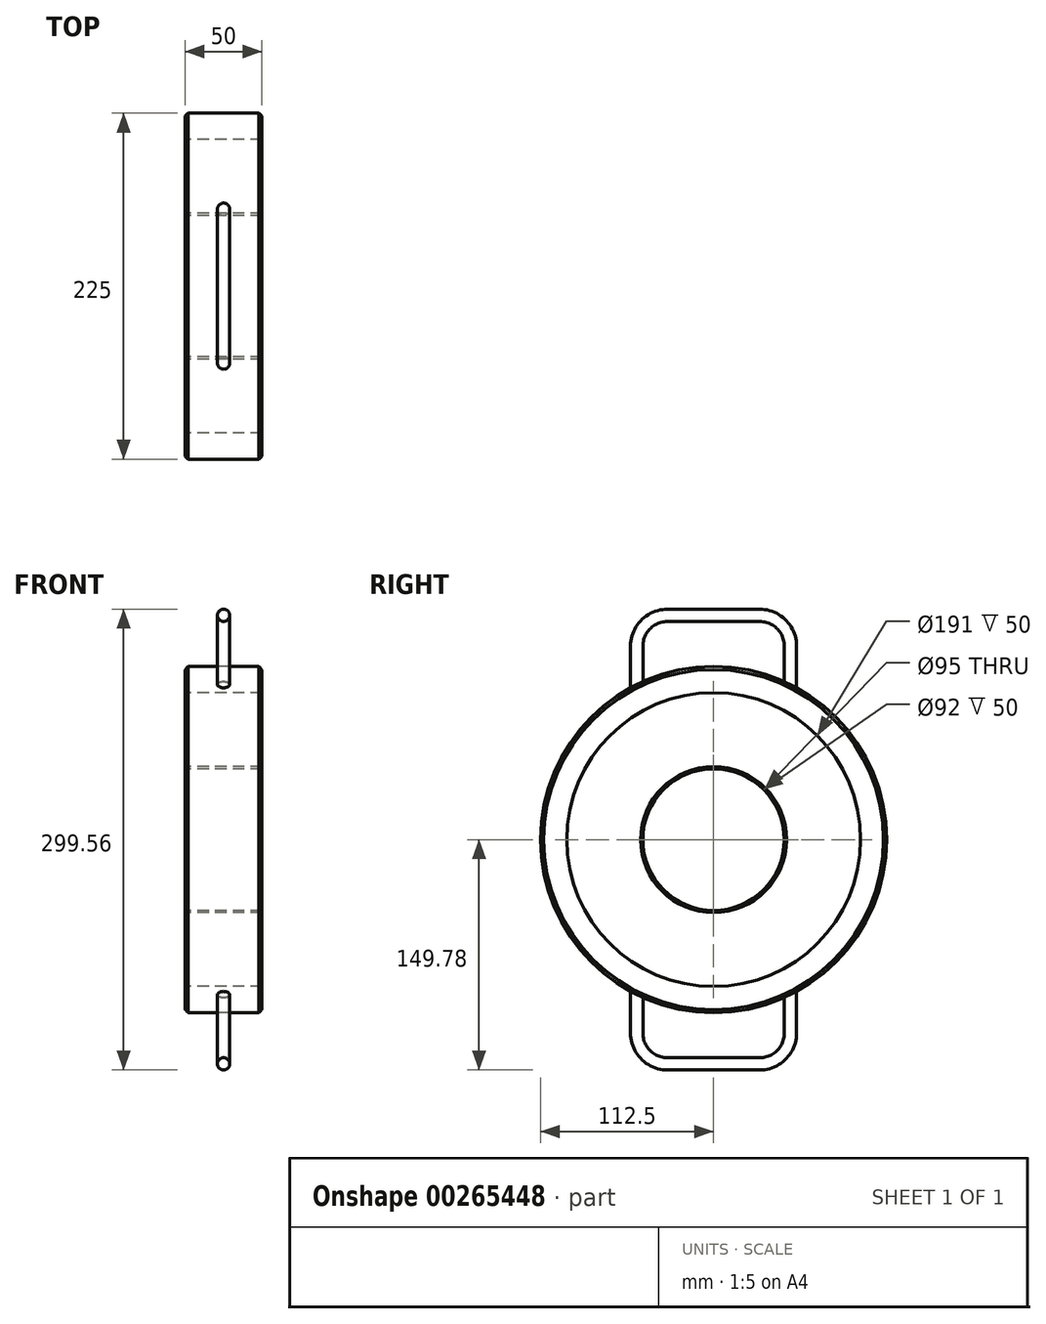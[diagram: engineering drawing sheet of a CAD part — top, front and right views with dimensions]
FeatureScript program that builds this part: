
annotation { "Feature Type Name" : "Feature", "Feature Type Description" : "" }
export const myFeature = defineFeature(function(context is Context, id is Id, definition is map)
    precondition{}
    {
        {
            var Q0;
            Q0=qCreatedBy(makeId("Front.planeOp"),FACE);
            var sketch = newSketch(context, id + "F0", { "sketchPlane" : qUnion([Q0])});
            skLineSegment(sketch, "E0", {"start": v(-48.97, 0) * mm, "end": v(48.97, 0) * mm, "construction": true});
            skLineSegment(sketch, "E1.bottom", {"start": v(-25, 47.5) * mm, "end": v(25, 47.5) * mm});
            skLineSegment(sketch, "E1.top", {"start": v(-25, 46) * mm, "end": v(25, 46) * mm});
            skLineSegment(sketch, "E1.left", {"start": v(-25, 47.5) * mm, "end": v(-25, 46) * mm});
            skLineSegment(sketch, "E1.right", {"start": v(25, 47.5) * mm, "end": v(25, 46) * mm});
            skLineSegment(sketch, "E2", {"start": v(0, 12.38) * mm, "end": v(0, -12.38) * mm, "construction": true});
            skSolve(sketch);
        }
        {
            var Q0;
            Q0=makeQuery(id+"F0.imprint","IMPRINT",FACE,{"disambiguationData":[TD([[makeQuery(id+"F0.imprint","IMPRINT",EDGE,{"derivedFrom":sQuery(id+"F0.wireOp",EDGE,"E1.bottom")}),-1.0]])]});
            var Q1;
            Q1=sQuery(id+"F0.wireOp",EDGE,"E0");
            revolve(context, id + "F1", {"entities" : qUnion([Q0]), "axis" : qUnion([Q1]), "revolveType" : RevolveType.FULL});
        }
        {
            var Q0;
            Q0=qCreatedBy(makeId("Front.planeOp"),FACE);
            var sketch = newSketch(context, id + "F2", { "sketchPlane" : qUnion([Q0])});
            skLineSegment(sketch, "E3.bottom", {"start": v(-25, 95.5) * mm, "end": v(25, 95.5) * mm});
            skLineSegment(sketch, "E3.top", {"start": v(-25, 47.5) * mm, "end": v(25, 47.5) * mm});
            skLineSegment(sketch, "E3.left", {"start": v(-25, 95.5) * mm, "end": v(-25, 47.5) * mm});
            skLineSegment(sketch, "E3.right", {"start": v(25, 95.5) * mm, "end": v(25, 47.5) * mm});
            skLineSegment(sketch, "E4", {"start": v(-46.04, 0) * mm, "end": v(46.04, 0) * mm, "construction": true});
            skSolve(sketch);
        }
        {
            var Q0;
            Q0=makeQuery(id+"F2.imprint","IMPRINT",FACE,{"disambiguationData":[TD([[makeQuery(id+"F2.imprint","IMPRINT",EDGE,{"derivedFrom":sQuery(id+"F2.wireOp",EDGE,"E3.bottom")}),-1.0]])]});
            var Q1;
            Q1=sQuery(id+"F2.wireOp",EDGE,"E4");
            revolve(context, id + "F3", {"entities" : qUnion([Q0]), "axis" : qUnion([Q1]), "revolveType" : RevolveType.FULL});
        }
        {
            var Q0;
            Q0=qCreatedBy(makeId("Front.planeOp"),FACE);
            var sketch = newSketch(context, id + "F4", { "sketchPlane" : qUnion([Q0])});
            skLineSegment(sketch, "E5", {"start": v(-40.4, 0) * mm, "end": v(40.4, 0) * mm, "construction": true});
            skLineSegment(sketch, "E6.bottom", {"start": v(-25, 112.5) * mm, "end": v(25, 112.5) * mm});
            skLineSegment(sketch, "E6.top", {"start": v(-25, 95.5) * mm, "end": v(25, 95.5) * mm});
            skLineSegment(sketch, "E6.left", {"start": v(-25, 112.5) * mm, "end": v(-25, 95.5) * mm});
            skLineSegment(sketch, "E6.right", {"start": v(25, 112.5) * mm, "end": v(25, 95.5) * mm});
            skSolve(sketch);
        }
        {
            var Q0;
            Q0=makeQuery(id+"F4.imprint","IMPRINT",FACE,{"disambiguationData":[TD([[makeQuery(id+"F4.imprint","IMPRINT",EDGE,{"derivedFrom":sQuery(id+"F4.wireOp",EDGE,"E6.bottom")}),-1.0]])]});
            var Q1;
            Q1=sQuery(id+"F4.wireOp",EDGE,"E5");
            revolve(context, id + "F5", {"entities" : qUnion([Q0]), "axis" : qUnion([Q1]), "revolveType" : RevolveType.FULL});
        }
        {
            var Q0;
            Q0=qCreatedBy(makeId("Right.planeOp"),FACE);
            var sketch = newSketch(context, id + "F6", { "sketchPlane" : qUnion([Q0])});
            skLineSegment(sketch, "E7", {"start": v(-50, 95.16) * mm, "end": v(-50, 125.78) * mm});
            skLineSegment(sketch, "E8", {"start": v(-30, 145.78) * mm, "end": v(30, 145.78) * mm});
            skLineSegment(sketch, "E9", {"start": v(50, 125.78) * mm, "end": v(50, 95.16) * mm});
            skPoint(sketch, "E10.visualSharp", {"position": v(50, 145.78) * mm});
            skArc(sketch, "E10.filletArc", {"start": v(50, 125.78) * mm, "mid": v(44.14, 139.92) * mm, "end": v(30, 145.78) * mm});
            skPoint(sketch, "E11.visualSharp", {"position": v(-50, 145.78) * mm});
            skArc(sketch, "E11.filletArc", {"start": v(-30, 145.78) * mm, "mid": v(-44.14, 139.92) * mm, "end": v(-50, 125.78) * mm});
            skPoint(sketch, "E12", {"position": v(50, 100.78) * mm});
            skSolve(sketch);
        }
        {
            var Q0;
            Q0=qCreatedBy(makeId("Top.planeOp"),FACE);
            var Q1;
            Q1=sQuery(id+"F6.wireOp",VERTEX,"E7.start");
            cPlane(context, id + "F7", {"entities" : qUnion([Q0, Q1]), "cplaneType" : CPlaneType.PLANE_POINT, "offset" : 25 * mm, "width" : 150 * mm, "height" : 150 * mm});
        }
        {
            var Q0;
            Q0=qCreatedBy(id+"F7.planeOp",FACE);
            var sketch = newSketch(context, id + "F8", { "sketchPlane" : qUnion([Q0])});
            skCircle(sketch, "E13", {"center": v(0, -50) * mm, "radius": 4 * mm});
            skSolve(sketch);
        }
        {
            var Q0;
            Q0=makeQuery(id+"F8.imprint","IMPRINT",FACE,{"disambiguationData":[TD([[makeQuery(id+"F8.imprint","IMPRINT",EDGE,{"derivedFrom":sQuery(id+"F8.wireOp",EDGE,"E13")}),1.0]])]});
            var Q1;
            Q1=sQuery(id+"F6.wireOp",EDGE,"E7");
            var Q2;
            Q2=sQuery(id+"F6.wireOp",EDGE,"E11.filletArc");
            var Q3;
            Q3=sQuery(id+"F6.wireOp",EDGE,"E8");
            var Q4;
            Q4=sQuery(id+"F6.wireOp",EDGE,"E10.filletArc");
            var Q5;
            Q5=sQuery(id+"F6.wireOp",EDGE,"E9");
            sweep(context, id + "F9", {"profiles" : qUnion([Q0]), "path" : qUnion([Q1, Q2, Q3, Q4, Q5])});
        }
        {
            var Q0;
            Q0=makeQuery(id+"F9.opSweep","SWEPT_BODY",BODY,{"disambiguationData":[OSD([sQuery(id+"F6.wireOp",EDGE,"E9"),sQuery(id+"F8.wireOp",EDGE,"E13")])]});
            var Q1;
            Q1=qCreatedBy(makeId("Top.planeOp"),FACE);
            mirror(context, id + "F10", {"operationType" : NewBodyOperationType.ADD, "entities" : qUnion([Q0]), "mirrorPlane" : qUnion([Q1])});
        }
        {
            var Q0;
            Q0=makeQuery(id+"F5.opRevolve","SWEPT_EDGE",EDGE,{"disambiguationData":[OSD([sQuery(id+"F4.wireOp",EDGE,"E6.bottom"),sQuery(id+"F4.wireOp",EDGE,"E6.right")])]});
            var Q1;
            Q1=makeQuery(id+"F5.opRevolve","SWEPT_EDGE",EDGE,{"disambiguationData":[OSD([sQuery(id+"F4.wireOp",EDGE,"E6.bottom"),sQuery(id+"F4.wireOp",EDGE,"E6.left")])]});
            chamfer(context, id + "F11", {"entities" : qUnion([Q0, Q1]), "width" : 2 * mm, "tangentPropagation" : true});
        }
    });
